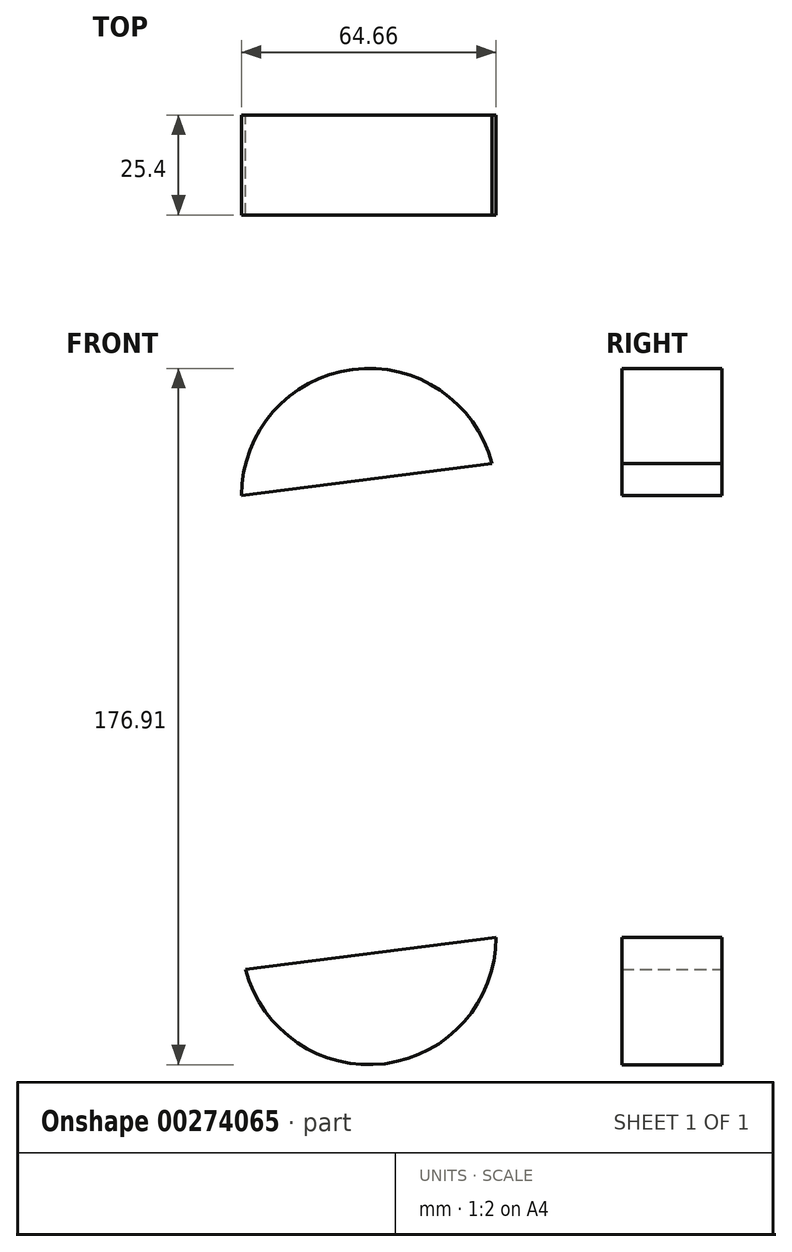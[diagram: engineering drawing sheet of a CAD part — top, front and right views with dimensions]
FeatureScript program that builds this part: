
annotation { "Feature Type Name" : "Feature", "Feature Type Description" : "" }
export const myFeature = defineFeature(function(context is Context, id is Id, definition is map)
    precondition{}
    {
        {
            var Q0;
            Q0=qCreatedBy(makeId("Front.planeOp"),FACE);
            var sketch = newSketch(context, id + "F0", { "sketchPlane" : qUnion([Q0])});
            skLineSegment(sketch, "E0", {"start": v(-31.3, -8.13) * mm, "end": v(32.33, 0) * mm});
            skLineSegment(sketch, "E1", {"start": v(31.3, 120.37) * mm, "end": v(-32.33, 112.25) * mm});
            skArc(sketch, "E2", {"start": v(-32.33, 112.25) * mm, "mid": v(-4.1, 144.32) * mm, "end": v(31.3, 120.37) * mm});
            skArc(sketch, "E3", {"start": v(32.33, 0) * mm, "mid": v(4.1, -32.07) * mm, "end": v(-31.3, -8.13) * mm});
            skSolve(sketch);
        }
        {
            var Q0;
            Q0=makeQuery(id+"F0.imprint","IMPRINT",FACE,{"disambiguationData":[TD([[makeQuery(id+"F0.imprint","IMPRINT",EDGE,{"derivedFrom":sQuery(id+"F0.wireOp",EDGE,"E0")}),-1.0]])]});
            var Q1;
            Q1=makeQuery(id+"F0.imprint","IMPRINT",FACE,{"disambiguationData":[TD([[makeQuery(id+"F0.imprint","IMPRINT",EDGE,{"derivedFrom":sQuery(id+"F0.wireOp",EDGE,"E1")}),-1.0]])]});
            extrude(context, id + "F1", {"entities" : qUnion([Q0, Q1]), "depth" : 25.4 * mm});
        }
    });
